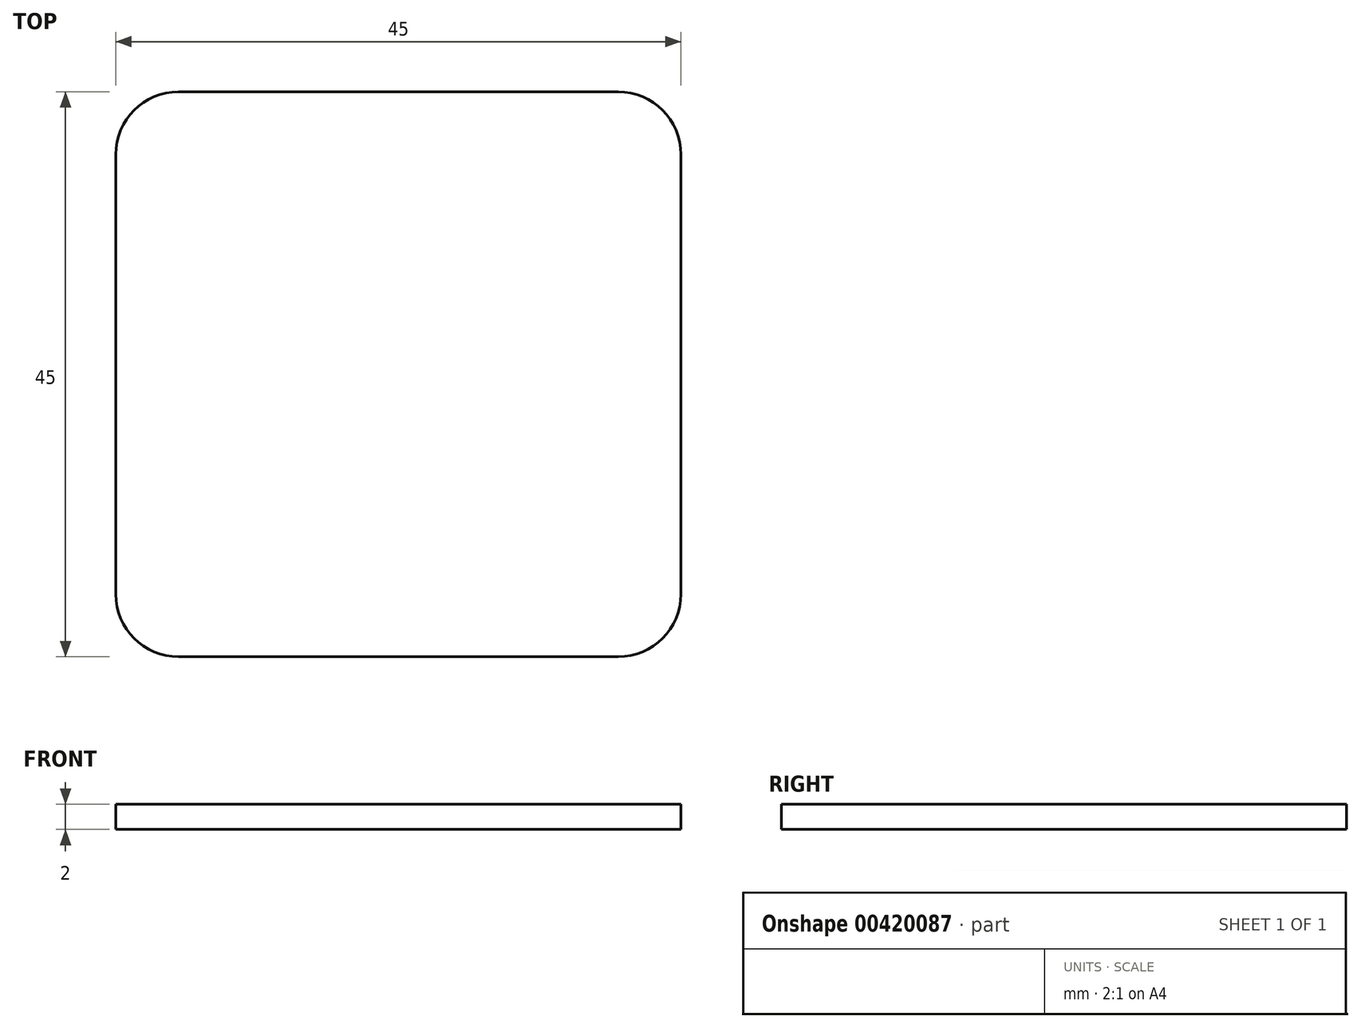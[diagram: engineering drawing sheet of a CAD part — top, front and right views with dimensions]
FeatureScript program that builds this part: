
annotation { "Feature Type Name" : "Feature", "Feature Type Description" : "" }
export const myFeature = defineFeature(function(context is Context, id is Id, definition is map)
    precondition{}
    {
        {
            var Q0;
            Q0=qCreatedBy(makeId("Top.planeOp"),FACE);
            var sketch = newSketch(context, id + "F0", { "sketchPlane" : qUnion([Q0])});
            skLineSegment(sketch, "E0.bottom", {"start": v(-22.5, -22.5) * mm, "end": v(22.5, -22.5) * mm});
            skLineSegment(sketch, "E0.top", {"start": v(-22.5, 22.5) * mm, "end": v(22.5, 22.5) * mm});
            skLineSegment(sketch, "E0.left", {"start": v(-22.5, -22.5) * mm, "end": v(-22.5, 22.5) * mm});
            skLineSegment(sketch, "E0.right", {"start": v(22.5, -22.5) * mm, "end": v(22.5, 22.5) * mm});
            skSolve(sketch);
        }
        {
            var Q0;
            Q0=makeQuery(id+"F0.imprint","IMPRINT",FACE,{"disambiguationData":[TD([[makeQuery(id+"F0.imprint","IMPRINT",EDGE,{"derivedFrom":sQuery(id+"F0.wireOp",EDGE,"E0.bottom")}),1.0]])]});
            extrude(context, id + "F1", {"entities" : qUnion([Q0]), "depth" : 2 * mm});
        }
        {
            var Q0;
            Q0=makeQuery(id+"F1.opExtrude","SWEPT_EDGE",EDGE,{"disambiguationData":[OSD([sQuery(id+"F0.wireOp",EDGE,"E0.bottom"),sQuery(id+"F0.wireOp",EDGE,"E0.left")])]});
            fillet(context, id + "F2", {"entities" : qUnion([Q0]), "radius" : 5 * mm, "tangentPropagation" : true, "allowEdgeOverflow" : false});
        }
        {
            var Q0;
            Q0=makeQuery(id+"F1.opExtrude","SWEPT_EDGE",EDGE,{"disambiguationData":[OSD([sQuery(id+"F0.wireOp",EDGE,"E0.bottom"),sQuery(id+"F0.wireOp",EDGE,"E0.right")])]});
            fillet(context, id + "F3", {"entities" : qUnion([Q0]), "radius" : 5 * mm, "tangentPropagation" : true, "allowEdgeOverflow" : false});
        }
        {
            var Q0;
            Q0=makeQuery(id+"F1.opExtrude","SWEPT_EDGE",EDGE,{"disambiguationData":[OSD([sQuery(id+"F0.wireOp",EDGE,"E0.top"),sQuery(id+"F0.wireOp",EDGE,"E0.right")])]});
            fillet(context, id + "F4", {"entities" : qUnion([Q0]), "radius" : 5 * mm, "tangentPropagation" : true, "allowEdgeOverflow" : false});
        }
        {
            var Q0;
            Q0=makeQuery(id+"F1.opExtrude","SWEPT_EDGE",EDGE,{"disambiguationData":[OSD([sQuery(id+"F0.wireOp",EDGE,"E0.top"),sQuery(id+"F0.wireOp",EDGE,"E0.left")])]});
            fillet(context, id + "F5", {"entities" : qUnion([Q0]), "radius" : 5 * mm, "tangentPropagation" : true, "allowEdgeOverflow" : false});
        }
    });
